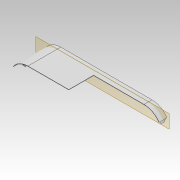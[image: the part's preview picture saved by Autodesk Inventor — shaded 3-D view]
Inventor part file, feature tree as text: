
AUTODESK INVENTOR PART (.ipt)
format: ipt  version: 2020 (Build 240168000, 168)  size: 221,696 bytes
history: native  units: mm
features: extrude x6, sketch x6, reference x5, other x5, projected_geometry x2, pattern_linear x1, fillet x1, plane x1, chamfer x1
ambient origin geometry x8: Origin, YZ Plane, XZ Plane, XY Plane, X Axis, Y Axis, Z Axis, Center Point
bodies: Solid1 (feature_tree)
feature tree (28):
  extrude  "Extrusion1"  Depth=68.0mm TaperAngle=0.0deg
  extrude  "Extrusion2"  Depth=2.0mm
  extrude  "Extrusion3"  Depth=20.0mm
  extrude  "Extrusion4"  Depth=4.0mm
  extrude  "Extrusion5"  Depth=11.8mm TaperAngle=0.0deg
  pattern_linear  "Rectangular Pattern1"  Spacing1=6.0mm  [1 undecoded]
  fillet  "Fillet1"  Radius=3.3mm
  plane  "Work Plane1"
  extrude  "Extrusion7"  Depth=12.0mm TaperAngle=0.0deg
  chamfer  "Chamfer1"  Distance=5.0mm
  sketch  "Sketch1"  dims[d0=21.8mm d1=0.0mm d2=68.0mm d3=0.0mm]
  reference  "Reference1"
  reference  "Reference2"
  reference  "Reference3"
  sketch  "Sketch2"  dims[d4=0.15mm d5=2.0mm]
  reference  "Reference4"
  projected_geometry  "Projected Loop1"
  sketch  "Sketch3"  dims[d6=12.0mm d7=20.0mm]
  reference  "Reference5"
  sketch  "Sketch4"  dims[d8=0.2mm d9=4.0mm]
  sketch  "Sketch5"  dims[d10=12.0mm d11=11.8mm d12=0.0mm]
  projected_geometry  "Projected Loop2"
  sketch  "Sketch7"  dims[d13=6.0mm d14=6.0mm d15=3.3mm d16=12.0mm d17=0.0mm d18=5.0mm d19=0.2mm d20=0.0mm d21=20.0mm d23=53.0mm d31=2.0mm d32=0.2mm d33=8.0mm d34=8.0mm d35=0.0mm d36=5.0mm d37=2.0mm d38=45.0deg]
  other  "<userpath>\Documents\Drew\Projects\OS-ARM\cad\FirstDraft\Link1.iam"
  other  "Link1.iam"
  other  "Link1a:1"
  other  "Link1b:1"
  other  "Link1c:1"
note: 1 required parameter value undecoded (feature->parameter linkage not recoverable at this tier; creation-order binding heuristic only, values carry confidence <= 0.55)
